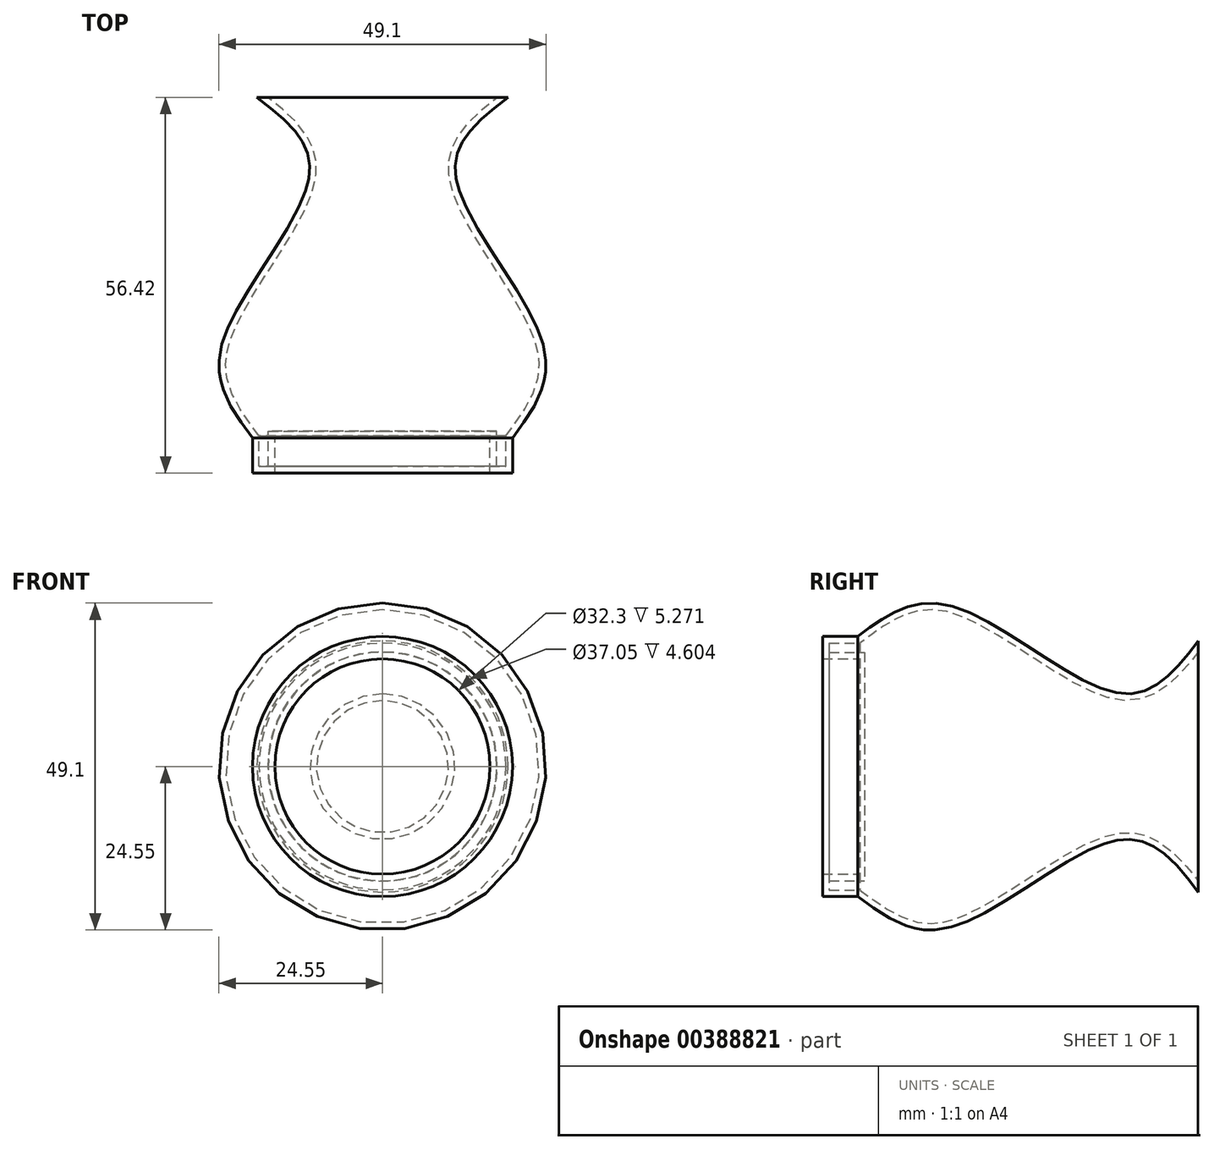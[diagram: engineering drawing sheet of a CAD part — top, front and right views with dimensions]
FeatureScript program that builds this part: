
annotation { "Feature Type Name" : "Feature", "Feature Type Description" : "" }
export const myFeature = defineFeature(function(context is Context, id is Id, definition is map)
    precondition{}
    {
        {
            var Q0;
            Q0=qCreatedBy(makeId("Top.planeOp"),FACE);
            var sketch = newSketch(context, id + "F0", { "sketchPlane" : qUnion([Q0])});
            skLineSegment(sketch, "E0", {"start": v(0, 0) * mm, "end": v(0, -51.15) * mm});
            skLineSegment(sketch, "E1", {"start": v(0, -51.15) * mm, "end": v(16.15, -51.15) * mm});
            skLineSegment(sketch, "E2", {"start": v(16.15, -51.15) * mm, "end": v(16.15, -56.42) * mm});
            skLineSegment(sketch, "E3", {"start": v(16.15, -56.42) * mm, "end": v(19.53, -56.42) * mm});
            skLineSegment(sketch, "E4", {"start": v(19.53, -56.42) * mm, "end": v(19.53, -51.15) * mm});
            skLineSegment(sketch, "E5", {"start": v(0, 0) * mm, "end": v(18.85, 0) * mm});
            skFitSpline(sketch, "E6", {"points": [v(18.85, 0) * mm, v(10.95, -11.5) * mm, v(24.24, -37.58) * mm, v(19.53, -51.15) * mm], "startDerivative": vector(-43.72, -33.75) * mm, "endDerivative": vector(-30.83, -41.2) * mm});
            skSolve(sketch);
        }
        {
            var Q0;
            Q0 = qSketchRegion(id + "F0", true);
            var Q1;
            Q1=sQuery(id+"F0.wireOp",EDGE,"E0");
            revolve(context, id + "F1", {"entities" : qUnion([Q0]), "axis" : qUnion([Q1]), "revolveType" : RevolveType.FULL});
        }
        {
            var Q0;
            Q0=makeQuery(id+"F1.opRevolve","SWEPT_FACE",FACE,{"disambiguationData":[OSD([sQuery(id+"F0.wireOp",EDGE,"E5")])]});
            shell(context, id + "F2", {"entities" : qUnion([Q0]), "thickness" : 1 * mm});
        }
    });
